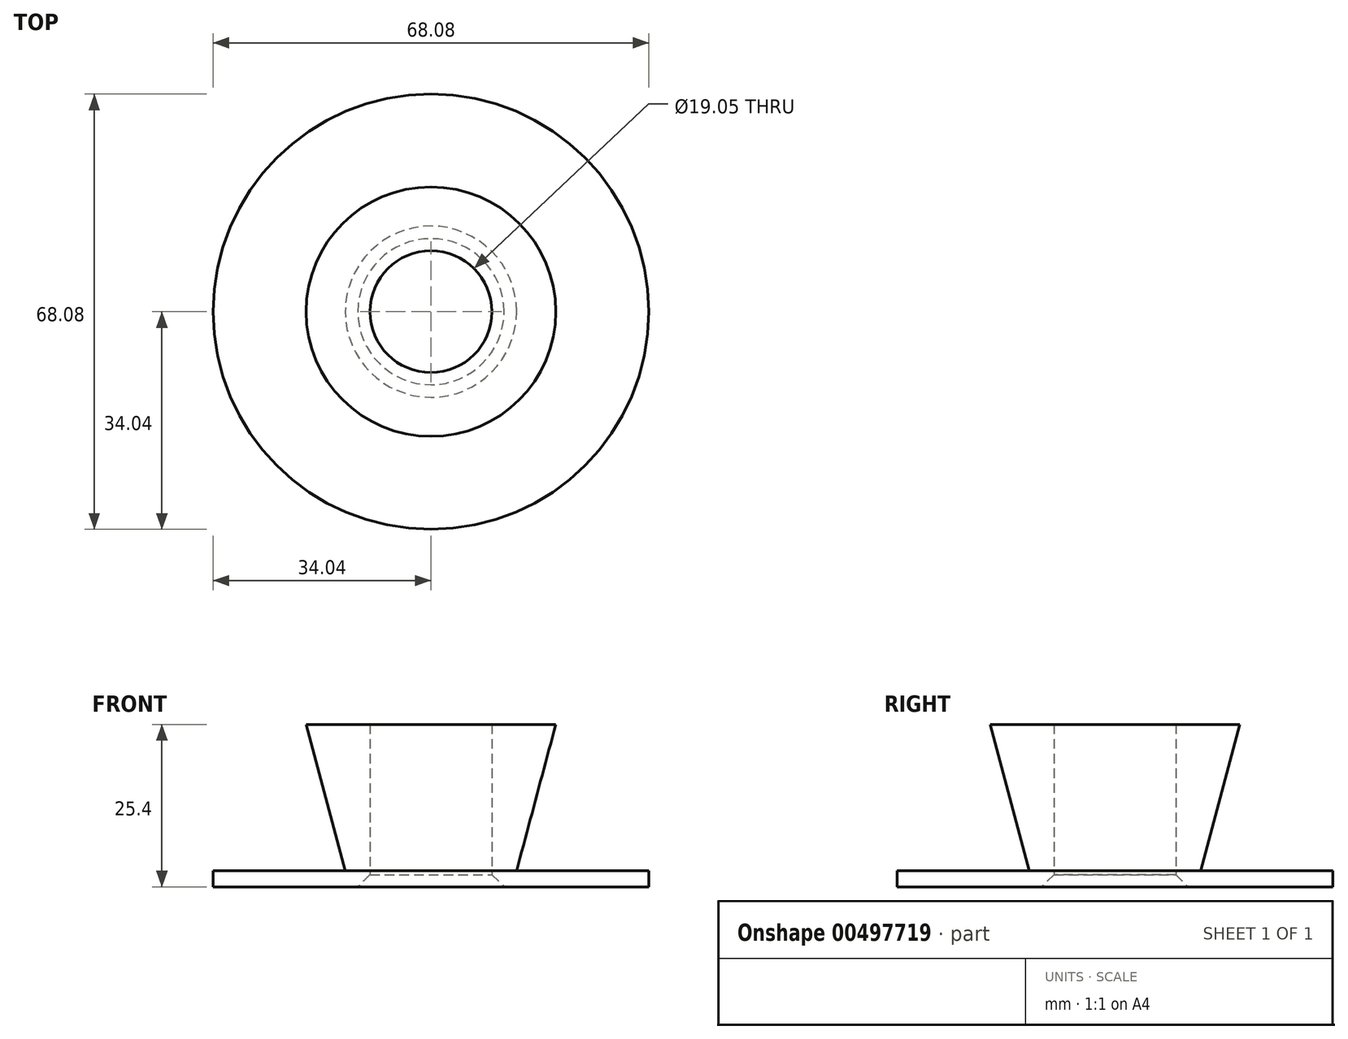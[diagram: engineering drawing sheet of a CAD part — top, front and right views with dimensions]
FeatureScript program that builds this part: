
annotation { "Feature Type Name" : "Feature", "Feature Type Description" : "" }
export const myFeature = defineFeature(function(context is Context, id is Id, definition is map)
    precondition{}
    {
        {
            var Q0;
            Q0=qCreatedBy(makeId("Top.planeOp"),FACE);
            var sketch = newSketch(context, id + "F0", { "sketchPlane" : qUnion([Q0])});
            skCircle(sketch, "E0", {"center": v(0, 0) * mm, "radius": 34.04 * mm});
            skCircle(sketch, "E1", {"center": v(0, 0) * mm, "radius": 6.35 * mm});
            skSolve(sketch);
        }
        {
            var Q0;
            Q0=makeQuery(id+"F0.imprint","IMPRINT",FACE,{"disambiguationData":[TD([[makeQuery(id+"F0.imprint","IMPRINT",EDGE,{"derivedFrom":sQuery(id+"F0.wireOp",EDGE,"E0")}),1.0]])]});
            extrude(context, id + "F1", {"entities" : qUnion([Q0]), "depth" : 2.54 * mm});
        }
        {
            var Q0;
            Q0=qCreatedBy(makeId("Top.planeOp"),FACE);
            var sketch = newSketch(context, id + "F2", { "sketchPlane" : qUnion([Q0])});
            skCircle(sketch, "E2", {"center": v(0, 0) * mm, "radius": 12.7 * mm});
            skSolve(sketch);
        }
        {
            var Q0;
            Q0=makeQuery(id+"F2.imprint","IMPRINT",FACE,{"disambiguationData":[TD([[makeQuery(id+"F2.imprint","IMPRINT",EDGE,{"derivedFrom":sQuery(id+"F2.wireOp",EDGE,"E2")}),1.0]])]});
            extrude(context, id + "F3", {"entities" : qUnion([Q0]), "operationType" : NewBodyOperationType.ADD, "depth" : 25.4 * mm, "hasDraft" : true, "draftAngle" : 15 * degree});
        }
        {
            var Q0;
            Q0=qCreatedBy(makeId("Top.planeOp"),FACE);
            var sketch = newSketch(context, id + "F4", { "sketchPlane" : qUnion([Q0])});
            skCircle(sketch, "E3", {"center": v(0, 0) * mm, "radius": 6.35 * mm});
            skSolve(sketch);
        }
        {
            var Q0;
            Q0=sQuery(id+"F4.wireOp",VERTEX,"E3.center");
            var Q1;
            Q1=makeQuery(id+"F1.opExtrude","SWEPT_BODY",BODY,{"disambiguationData":[OSD([sQuery(id+"F0.wireOp",EDGE,"E0"),sQuery(id+"F0.wireOp",EDGE,"E1")])]});
            hole(context, id + "F5", {"style" : HoleStyle.C_SINK, "endStyle" : HoleEndStyle.THROUGH, "oppositeDirection" : true, "holeDiameter" : 19.05 * mm, "cSinkDiameter" : 22.86 * mm, "cSinkAngle" : 90 * degree, "isTappedThrough" : true, "tappedDepth" : 12.7 * mm, "tapClearance" : 3, "locations" : qUnion([Q0]), "scope" : qUnion([Q1])});
        }
    });
